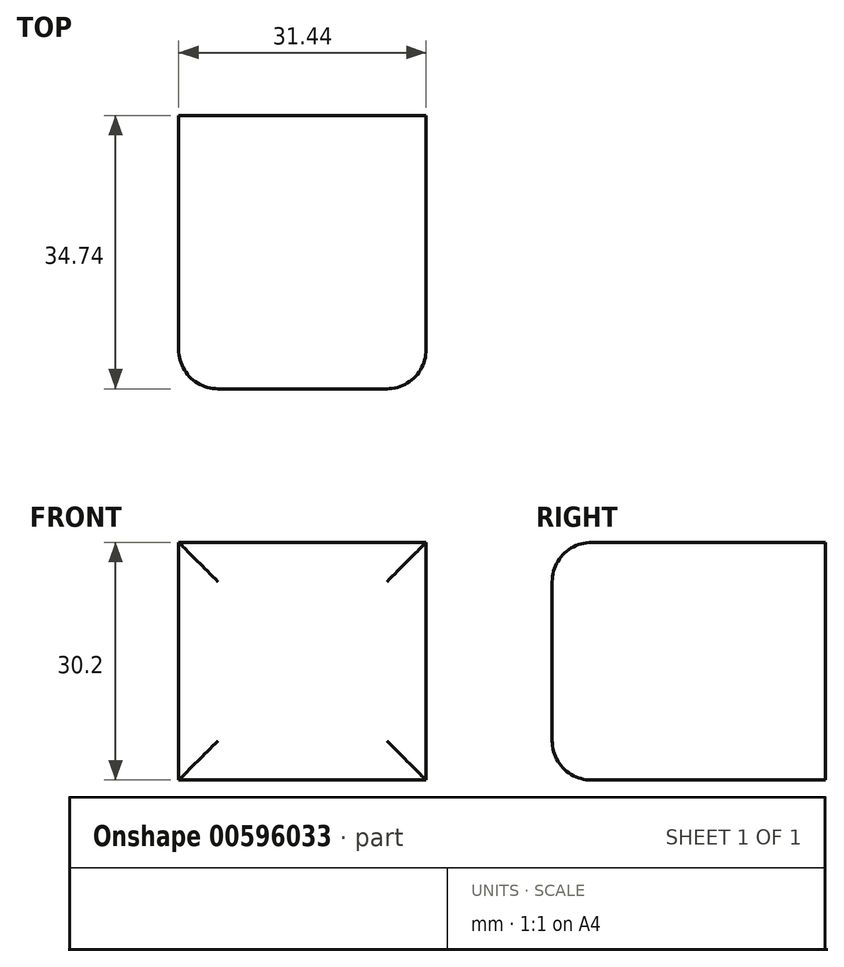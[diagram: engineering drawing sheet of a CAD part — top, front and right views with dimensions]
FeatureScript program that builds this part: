
annotation { "Feature Type Name" : "Feature", "Feature Type Description" : "" }
export const myFeature = defineFeature(function(context is Context, id is Id, definition is map)
    precondition{}
    {
        {
            var Q0;
            Q0=qCreatedBy(makeId("Top.planeOp"),FACE);
            var sketch = newSketch(context, id + "F0", { "sketchPlane" : qUnion([Q0])});
            skLineSegment(sketch, "E0.bottom", {"start": v(15.72, 17.37) * mm, "end": v(-15.72, 17.37) * mm});
            skLineSegment(sketch, "E0.top", {"start": v(15.72, -17.37) * mm, "end": v(-15.72, -17.37) * mm});
            skLineSegment(sketch, "E0.left", {"start": v(15.72, 17.37) * mm, "end": v(15.72, -17.37) * mm});
            skLineSegment(sketch, "E0.right", {"start": v(-15.72, 17.37) * mm, "end": v(-15.72, -17.37) * mm});
            skPoint(sketch, "E0.middle", {"position": v(0, 0) * mm});
            skSolve(sketch);
        }
        {
            var Q0;
            Q0 = qSketchRegion(id + "F0", true);
            extrude(context, id + "F1", {"entities" : qUnion([Q0]), "depth" : 30.2 * mm, "offsetDistance" : 25 * mm});
        }
        {
            var Q0;
            Q0=makeQuery(id+"F1.opExtrude","SWEPT_FACE",FACE,{"disambiguationData":[OSD([sQuery(id+"F0.wireOp",EDGE,"E0.top")])]});
            fillet(context, id + "F2", {"entities" : qUnion([Q0]), "radius" : 5 * mm, "tangentPropagation" : true, "allowEdgeOverflow" : false});
        }
    });
